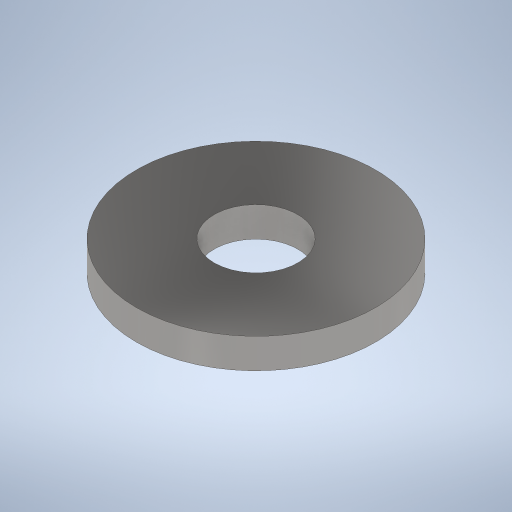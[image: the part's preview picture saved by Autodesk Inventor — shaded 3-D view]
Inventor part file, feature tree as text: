
AUTODESK INVENTOR PART (.ipt)
format: ipt  version: 2024.2 (Build 282272000, 272)  size: 243,712 bytes
history: native  units: mm
features: revolve x1, sketch x1
ambient origin geometry x8: Origin, YZ Plane, XZ Plane, XY Plane, X Axis, Y Axis, Z Axis, Center Point
bodies: Solid1 (feature_tree)
feature tree (2):
  revolve  "Revolution1"  [1 undecoded]
  sketch  "Sketch1"  dims[d5=90.0deg]
note: 1 required parameter value undecoded (feature->parameter linkage not recoverable at this tier; creation-order binding heuristic only, values carry confidence <= 0.55)
